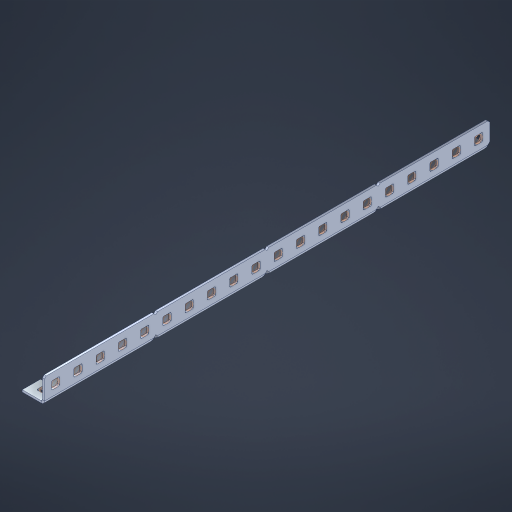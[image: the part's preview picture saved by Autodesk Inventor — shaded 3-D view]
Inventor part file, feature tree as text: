
AUTODESK INVENTOR PART (.ipt)
format: ipt  version: 2023 (Build 270158000, 158)  size: 951,296 bytes
history: native  units: in
note: dims shown in document units (in); Inventor stores cm internally (conversion verified against a paired STEP export)
features: other x67, extrude x58, sheet_metal_op x11, sketch x10, pattern_linear x2, mirror x1, chamfer x1
ambient origin geometry x8: Origin, YZ Plane, XZ Plane, XY Plane, X Axis, Y Axis, Z Axis, Center Point
bodies: Solid1 (feature_tree), Body (feature_tree)
feature tree (150):
  sheet_metal_op  "Flanges"
  other  "Flange Pattern Plane"
  other  "Flange Pattern Sketch"
  sheet_metal_op  "Flange Pattern"
  sheet_metal_op  "Body Pattern"
  pattern_linear  "Center Pattern"  Spacing1=0.0469in  [1 undecoded]
  other  "Arc Length"
  mirror  "Notch Mirror"
  pattern_linear  "Notch Pattern"  Spacing1=0.182in  [1 undecoded]
  chamfer  "End Chamfer"
  extrude  "Half Cut"  Depth=0.02in
  sketch  "Sketch1"  dims[d0=1.0in]
  other  "Plate1"
  sketch  "Sketch2"  dims[d1=10.0in]
  other  "Plate2"
  sheet_metal_op  "Bend1"
  sheet_metal_op  "Corner1"
  sketch  "Sketch3"  dims[d2=0.0469in]
  sketch  "Sketch7"  dims[d3=0.0469in]
  other  "Srf1"
  other  "Srf2"
  sketch  "Sketch8"  dims[d4=0.0234in]
  sketch  "Sketch9"  dims[d5=0.0938in]
  other  "Srf91"
  sheet_metal_op  "Body Pattern Sketch"
  other  "Srf92"
  sketch  "Sketch13"  dims[d6=0.0469in]
  sketch  "Sketch14"  dims[d7=0.5in d8=90.0deg d9=0.0312in]
  sketch  "Sketch15"  dims[d10=0.1875in]
  sketch  "Sketch16"  dims[d11=0.0469in d12=0.0469in d16=0.182in d17=0.02in d18=0.0469in d19=0.0in d20=0.25in d21=0.25in d38=7.874in d40=0.5in d41=0.3937in d43=1.0in d46=0.172in d47=1.0in d48=0.0in d49=0.182in d50=0.02in d51=0.25in d52=0.25in d53=0.0469in d54=0.0in d55=0.172in d56=1.0in d57=0.0in d58=0.25in d60=7.874in d62=0.5in d63=0.3937in d65=0.5in d85=0.1227in d86=0.1659in d88=0.04in d89=0.0469in d90=0.0in d91=0.04in d92=0.0491in d95=2.5in d96=0.04in d97=0.25in d98=45.0deg d99=0.25in d100=0.5in d101=0.0in d102=2.497in d106=0.182in d107=0.02in d108=0.5in d109=0.5in d110=0.0469in d111=0.0in d112=0.172in d113=0.5in d114=0.0in d117=0.5in d118=0.5in d119=0.5in]
  other  "Srf786"
  other  "Srf823"
  other  "Srf824"
  other  "Srf825"
  other  "Srf826"
  other  "Srf827"
  other  "Srf828"
  other  "Srf829"
  other  "Srf856"
  other  "Srf857"
  other  "Srf858"
  other  "Srf859"
  other  "Srf860"
  other  "Srf861"
  other  "Srf862"
  other  "Srf889"
  other  "Srf890"
  other  "Srf891"
  other  "Srf892"
  other  "Srf893"
  other  "Srf894"
  other  "Srf895"
  other  "Srf896"
  other  "Srf922"
  other  "Srf923"
  other  "Srf924"
  other  "Srf925"
  other  "Srf926"
  other  "Srf959"
  other  "Srf960"
  other  "Srf961"
  other  "Srf962"
  other  "Srf963"
  other  "Srf996"
  other  "Srf997"
  other  "Srf998"
  other  "Srf999"
  other  "Srf1000"
  other  "Srf1143"
  other  "Srf1144"
  other  "Srf1145"
  other  "Srf1146"
  other  "Srf1147"
  other  "Srf1148"
  other  "Srf1199"
  other  "Srf1200"
  other  "Srf1201"
  other  "Srf1202"
  other  "Srf1203"
  other  "Srf1204"
  other  "Srf1255"
  other  "Srf1256"
  other  "Srf1257"
  other  "Srf1258"
  other  "Srf1259"
  other  "Srf1260"
  sheet_metal_op  "Flange Stamp"
  sheet_metal_op  "Flange Circle"
  sheet_metal_op  "Body Stamp"
  sheet_metal_op  "Body Circle"
  other  "Center Stamp"
  other  "Center Circle"
  sheet_metal_op  "Notch"
  extrude  "ExtrusionSrf2"  Depth=0.0469in
  extrude  "ExtrusionSrf92"  TaperAngle=0.0deg  [1 undecoded]
  extrude  "ExtrusionSrf823"  Depth=0.25in
  extrude  "ExtrusionSrf824"  Depth=0.25in
  extrude  "ExtrusionSrf825"  Depth=0.5in
  extrude  "ExtrusionSrf826"  Depth=0.5in
  extrude  "ExtrusionSrf827"  Depth=1.0in TaperAngle=0.0deg
  extrude  "ExtrusionSrf828"  Depth=0.182in
  extrude  "ExtrusionSrf829"  Depth=0.02in
  extrude  "ExtrusionSrf856"  Depth=0.25in
  extrude  "ExtrusionSrf857"  Depth=0.25in
  extrude  "ExtrusionSrf858"  Depth=0.0469in
  extrude  "ExtrusionSrf859"  TaperAngle=0.0deg  [1 undecoded]
  extrude  "ExtrusionSrf860"  Depth=0.5in
  extrude  "ExtrusionSrf861"  Depth=1.0in TaperAngle=0.0deg
  extrude  "ExtrusionSrf862"  Depth=0.25in
  extrude  "ExtrusionSrf889"  Depth=0.5in
  extrude  "ExtrusionSrf890"  Depth=0.5in
  extrude  "ExtrusionSrf891"  Depth=0.5in
  extrude  "ExtrusionSrf892"  Depth=0.5in
  extrude  "ExtrusionSrf893"  Depth=0.5in
  extrude  "ExtrusionSrf894"  Depth=0.0469in
  extrude  "ExtrusionSrf895"  TaperAngle=0.0deg  [1 undecoded]
  extrude  "ExtrusionSrf896"  Depth=0.5in
  extrude  "ExtrusionSrf922"  Depth=0.5in
  extrude  "ExtrusionSrf923"  Depth=2.5in
  extrude  "ExtrusionSrf924"  Depth=0.25in TaperAngle=45.0deg
  extrude  "ExtrusionSrf925"  Depth=0.25in
  extrude  "ExtrusionSrf926"  Depth=0.5in TaperAngle=0.0deg
  extrude  "ExtrusionSrf959"  Depth=0.5in
  extrude  "ExtrusionSrf960"  Depth=0.182in
  extrude  "ExtrusionSrf961"  Depth=0.02in
  extrude  "ExtrusionSrf962"  Depth=0.5in
  extrude  "ExtrusionSrf963"  Depth=0.5in
  extrude  "ExtrusionSrf996"  Depth=0.0469in
  extrude  "ExtrusionSrf997"  TaperAngle=0.0deg  [1 undecoded]
  extrude  "ExtrusionSrf998"  Depth=0.5in
  extrude  "ExtrusionSrf999"  Depth=0.5in TaperAngle=0.0deg
  extrude  "ExtrusionSrf1000"  Depth=0.5in
  extrude  "ExtrusionSrf1143"  Depth=0.5in
  extrude  "ExtrusionSrf1144"  Depth=0.5in
  extrude  "ExtrusionSrf1145"  [1 undecoded]
  extrude  "ExtrusionSrf1146"  [1 undecoded]
  extrude  "ExtrusionSrf1147"  [1 undecoded]
  extrude  "ExtrusionSrf1148"  [1 undecoded]
  extrude  "ExtrusionSrf1199"  [1 undecoded]
  extrude  "ExtrusionSrf1200"  [1 undecoded]
  extrude  "ExtrusionSrf1201"  [1 undecoded]
  extrude  "ExtrusionSrf1202"  [1 undecoded]
  extrude  "ExtrusionSrf1203"  [1 undecoded]
  extrude  "ExtrusionSrf1204"  [1 undecoded]
  extrude  "ExtrusionSrf1255"  [1 undecoded]
  extrude  "ExtrusionSrf1256"  [1 undecoded]
  extrude  "ExtrusionSrf1257"  [1 undecoded]
  extrude  "ExtrusionSrf1258"  [1 undecoded]
  extrude  "ExtrusionSrf1259"  [1 undecoded]
  extrude  "ExtrusionSrf1260"  [1 undecoded]
note: 22 required parameter values undecoded (feature->parameter linkage not recoverable at this tier; creation-order binding heuristic only, values carry confidence <= 0.55)
